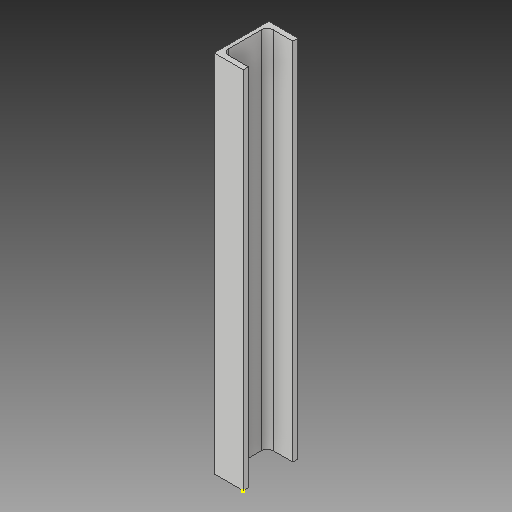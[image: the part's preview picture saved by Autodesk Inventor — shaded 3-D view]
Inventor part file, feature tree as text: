
AUTODESK INVENTOR PART (.ipt)
format: ipt  version: 2019 (Build 230136000, 136)  size: 96,768 bytes
history: native  units: in
note: dims shown in document units (in); Inventor stores cm internally (conversion verified against a paired STEP export)
features: other x3, sketch x2
ambient origin geometry x8: Origin, YZ Plane, XZ Plane, XY Plane, X Axis, Y Axis, Z Axis, Center Point
bodies: Solid1 (feature_tree)
feature tree (5):
  other  "Channel2_MIR.ipt"
  other  "Solid1::Channel2_MIR.ipt"
  other  "TaggingFeature1"
  sketch  "Sketch1"  dims[d0=0.3937in]
  sketch  "Sketch2"
